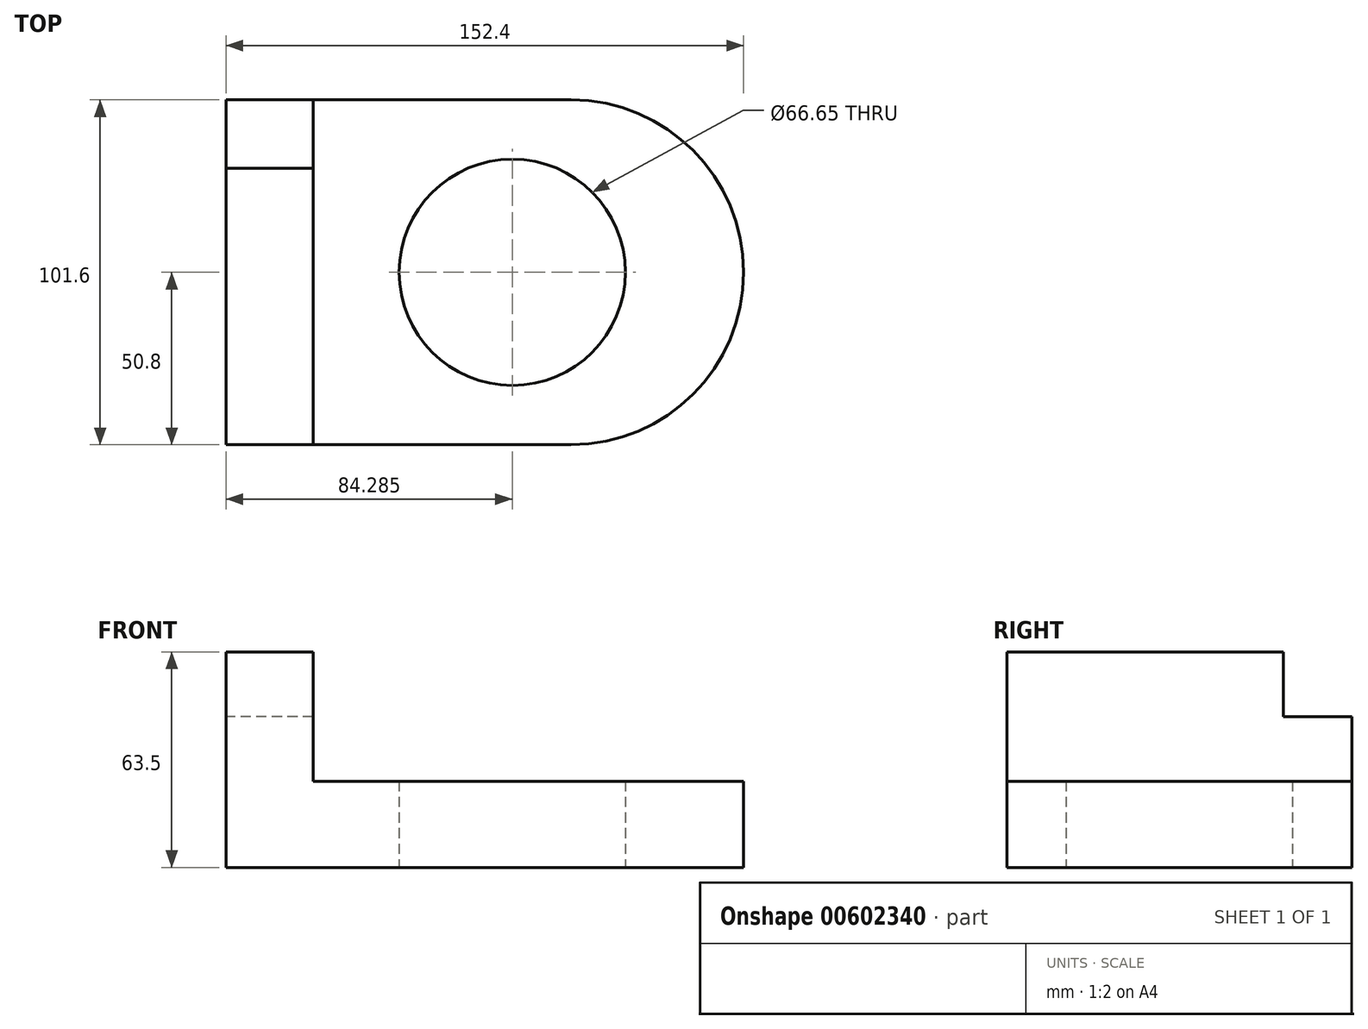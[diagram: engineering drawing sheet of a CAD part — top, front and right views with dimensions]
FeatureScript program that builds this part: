
annotation { "Feature Type Name" : "Feature", "Feature Type Description" : "" }
export const myFeature = defineFeature(function(context is Context, id is Id, definition is map)
    precondition{}
    {
        {
            var Q0;
            Q0=qCreatedBy(makeId("Top.planeOp"),FACE);
            var sketch = newSketch(context, id + "F0", { "sketchPlane" : qUnion([Q0])});
            skLineSegment(sketch, "E0.bottom", {"start": v(-50.8, 50.8) * mm, "end": v(50.8, 50.8) * mm});
            skLineSegment(sketch, "E0.top", {"start": v(-50.8, -50.8) * mm, "end": v(50.8, -50.8) * mm});
            skLineSegment(sketch, "E0.left", {"start": v(-50.8, 50.8) * mm, "end": v(-50.8, -50.8) * mm});
            skLineSegment(sketch, "E0.right", {"start": v(50.8, 50.8) * mm, "end": v(50.8, -50.8) * mm});
            skPoint(sketch, "E0.middle", {"position": v(0, 0) * mm});
            skArc(sketch, "E1", {"start": v(50.8, -50.8) * mm, "mid": v(101.6, 0) * mm, "end": v(50.8, 50.8) * mm});
            skSolve(sketch);
        }
        {
            var Q0;
            Q0=makeQuery(id+"F0.imprint","IMPRINT",FACE,{"disambiguationData":[TD([[makeQuery(id+"F0.imprint","IMPRINT",EDGE,{"derivedFrom":sQuery(id+"F0.wireOp",EDGE,"E0.bottom")}),-1.0]])]});
            var sketch = newSketch(context, id + "F1", { "sketchPlane" : qUnion([Q0])});
            skCircle(sketch, "E2", {"center": v(33.48, 0) * mm, "radius": 33.33 * mm});
            skSolve(sketch);
        }
        {
            var Q0;
            Q0=makeQuery(id+"F0.imprint","IMPRINT",FACE,{"disambiguationData":[TD([[makeQuery(id+"F0.imprint","IMPRINT",EDGE,{"derivedFrom":sQuery(id+"F0.wireOp",EDGE,"E0.bottom")}),-1.0]])]});
            var Q1;
            Q1=makeQuery(id+"F0.imprint","IMPRINT",FACE,{"disambiguationData":[TD([[makeQuery(id+"F0.imprint","IMPRINT",EDGE,{"derivedFrom":sQuery(id+"F0.wireOp",EDGE,"E0.right")}),1.0]])]});
            extrude(context, id + "F2", {"entities" : qUnion([Q0, Q1]), "depth" : 25.4 * mm, "offsetDistance" : 25.4 * mm});
        }
        {
            var Q0;
            {var subQ0=sQuery(id+"F1.wireOp",EDGE,"E2");var subQ1=makeQuery(id+"F0.imprint","IMPRINT",EDGE,{"derivedFrom":sQuery(id+"F0.wireOp",EDGE,"E0.right")});var subQ2=makeQuery(id+"F1.imprint","INTERSECT",VERTEX,{"disambiguationData":[OD(0.0)],"derivedFrom":[subQ1,subQ0]});Q0=makeQuery(id+"F1.imprint","IMPRINT",FACE,{"disambiguationData":[TD([[makeQuery(id+"F1.imprint","IMPRINT",EDGE,{"disambiguationData":[TD([[subQ2,-1.0]])],"derivedFrom":subQ0}),1.0]])]});}
            var Q1;
            {var subQ0=sQuery(id+"F1.wireOp",EDGE,"E2");var subQ1=makeQuery(id+"F0.imprint","IMPRINT",EDGE,{"derivedFrom":sQuery(id+"F0.wireOp",EDGE,"E0.right")});var subQ2=makeQuery(id+"F1.imprint","INTERSECT",VERTEX,{"disambiguationData":[OD(0.0)],"derivedFrom":[subQ1,subQ0]});Q1=makeQuery(id+"F1.imprint","IMPRINT",FACE,{"disambiguationData":[TD([[makeQuery(id+"F1.imprint","IMPRINT",EDGE,{"disambiguationData":[TD([[subQ2,1.0]])],"derivedFrom":subQ0}),1.0]])]});}
            var Q2;
            Q2=sQuery(id+"F1.wireOp",EDGE,"E2");
            extrude(context, id + "F3", {"entities" : qUnion([Q0, Q1]), "operationType" : NewBodyOperationType.REMOVE, "surfaceEntities" : qUnion([Q2]), "depth" : 54.86 * mm, "offsetDistance" : 25.4 * mm});
        }
        {
            var Q0;
            Q0=makeQuery(id+"F2.opExtrude","SWEPT_FACE",FACE,{"disambiguationData":[OSD([sQuery(id+"F0.wireOp",EDGE,"E0.left")])]});
            var sketch = newSketch(context, id + "F4", { "sketchPlane" : qUnion([Q0])});
            skLineSegment(sketch, "E3.bottom", {"start": v(-50.8, 44.45) * mm, "end": v(50.8, 44.45) * mm});
            skLineSegment(sketch, "E3.top", {"start": v(-50.8, 25.4) * mm, "end": v(50.8, 25.4) * mm});
            skLineSegment(sketch, "E3.left", {"start": v(-50.8, 44.45) * mm, "end": v(-50.8, 25.4) * mm});
            skLineSegment(sketch, "E3.right", {"start": v(50.8, 44.45) * mm, "end": v(50.8, 25.4) * mm});
            skLineSegment(sketch, "E4.bottom", {"start": v(-30.58, 63.5) * mm, "end": v(50.8, 63.5) * mm});
            skLineSegment(sketch, "E4.top", {"start": v(-30.58, 44.45) * mm, "end": v(50.8, 44.45) * mm});
            skLineSegment(sketch, "E4.left", {"start": v(-30.58, 63.5) * mm, "end": v(-30.58, 44.45) * mm});
            skLineSegment(sketch, "E4.right", {"start": v(50.8, 63.5) * mm, "end": v(50.8, 44.45) * mm});
            skSolve(sketch);
        }
        {
            var Q0;
            Q0=makeQuery(id+"F4.imprint","IMPRINT",FACE,{"disambiguationData":[TD([[makeQuery(id+"F4.imprint","IMPRINT",EDGE,{"derivedFrom":sQuery(id+"F4.wireOp",EDGE,"E4.bottom")}),-1.0]])]});
            var Q1;
            Q1=makeQuery(id+"F4.imprint","IMPRINT",FACE,{"disambiguationData":[TD([[makeQuery(id+"F4.imprint","IMPRINT",EDGE,{"derivedFrom":sQuery(id+"F4.wireOp",EDGE,"E3.bottom")}),-1.0]])]});
            extrude(context, id + "F5", {"entities" : qUnion([Q0, Q1]), "operationType" : NewBodyOperationType.ADD, "oppositeDirection" : true, "depth" : 25.65 * mm, "offsetDistance" : 25.4 * mm});
        }
    });
